# Revit family: ASH_ArmitageShanks_WCSeats_Contour21_Splash305SeatOnly
name_source: partatom
category: Plumbing Fixtures
revit_build: Autodesk Revit MEP 2012 (Build: 20110309_2315(x64)
units: mm (PartAtom-declared; Revit-internal decimal feet)

## types (4) — shared parameters
Accessories = www.idealspec.co.uk
AreaUnits = millimeters
Assembly Code = C1030200
AssetType = Fixed
BIMObjectName = ASH_ArmitageShanks_WCSeats_Contour21Splash_S4542
Brand = Armitage Shanks
ConnectionType = Mechanical
Default Elevation = 1219 mm
Description = Contour 21 splash seat ring only for 305 mm bowls
DurationUnit = year
ECA = No
ExpectedLife = 15
Features = Seat ring only for 305 mm bowls
Help = www.idealspec.co.uk/contact-us.html
IfcExportAs = IfcSanitaryTerminalType
IfcExportType = WCSEAT
InstallationInstructions = www.idealspec.co.uk/resources.html
LinearUnits = millimeters
ManufacturerURL = www.idealspec.co.uk
Material = Plastic
ModelReference = Contour 21 splash seat ring only for 305 mm bowls
NBSDescription = WC seats and covers
NBSReference = 45-35-70/391
Name = WCSeats_Contour21Splash-S4542_ArmitageShanks
NettWeight = 1.20 kg
NominalDepth = 398 mm
NominalLength = 398 mm
NominalWidth = 400 mm  [stored 1.31234 ft]
SeatColor = White
SeatHasCover = No
SeatMaterial = Plastic
SeatType = RingSeat
Shape = Sculptured
Space = Internal
SpareParts = www.fastpart-spares.co.uk
URL = www.idealspec.co.uk
Uniclass2 = Pr_40_20_93_95
Version = 2
VolumeUnits = Litres
WRAS = No
WarrantyDescription = Manufacturers Warranty
WarrantyDurationParts = 5
WarrantyDurationUnit = year
WaterEfficientProduct = No
zero-valued in all types: CWFU, Cost, HWFU, WFU

## per-type parameters (varying)
| type | Color | Finish | Model | ModelNumber | NominalHeight | ProductInformation | SeatSKU | Size |
| S454201-Contour 21 Splash seat ring only for 305mm bowls - White | White | White | S454201 | S454201 | 0 mm  [stored 0 ft] | www.idealspec.co.uk/assets/datasheet/S454201 | ASH_ArmitageShanks _WC_White1_Render | x x mm |
| S454236-Contour 21 Splash seat ring only for 305mm bowls - Blue | Blue | Blue | S454236 | S454236 | 0 mm  [stored 0 ft] | www.idealspec.co.uk/assets/datasheet/S454236 | ASH_ArmitageShanks _WC_Blue_Render | x x mm |
| S4542GQ-Contour 21 Splash seat ring only for 305mm bowls - Red | Red | Red | S4542GQ | S4542GQ | 58 mm | www.idealspec.co.uk/assets/datasheet/S4542GQ | ASH_ArmitageShanks _WC_Red_Render | 400 x 400 x 60 mm |
| S454279-Contour 21 Splash seat ring only for 305mm bowls - Yellow | Yellow | Yellow | S454279 | S454279 | 0 mm  [stored 0 ft] | www.idealspec.co.uk/assets/datasheet/S454279 | ASH_ArmitageShanks _WCSeat_Yellow_Render | x x mm |

note: [stored X ft] marks values corroborated as IEEE doubles in the binary element streams (Revit-internal decimal feet)
